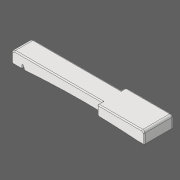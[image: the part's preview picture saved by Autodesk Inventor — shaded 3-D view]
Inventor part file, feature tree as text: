
AUTODESK INVENTOR PART (.ipt)
format: ipt  version: 2020 (Build 240168000, 168)  size: 305,664 bytes
history: native  units: in
note: dims shown in document units (in); Inventor stores cm internally (conversion verified against a paired STEP export)
features: other x4, extrude x4, fillet x2
ambient origin geometry x8: Origin, YZ Plane, XZ Plane, XY Plane, X Axis, Y Axis, Z Axis, Center Point
bodies: Solid1 (feature_tree)
feature tree (10):
  other  "DKey0"
  other  "Slot Start Plane"
  other  "Key Profile"
  extrude  "Upper"  TaperAngle=0.0deg  [1 undecoded]
  extrude  "Lower"  TaperAngle=0.0deg  [1 undecoded]
  extrude  "Protrusion Cutout"  Depth=0.0591in
  fillet  "Front Fillet"  Radius=0.1374in
  extrude  "Slot"  [1 undecoded]
  fillet  "Edge Softening"  Radius=0.0787in
  other  "Slot Sketch"
note: 3 required parameter values undecoded (feature->parameter linkage not recoverable at this tier; creation-order binding heuristic only, values carry confidence <= 0.55)
